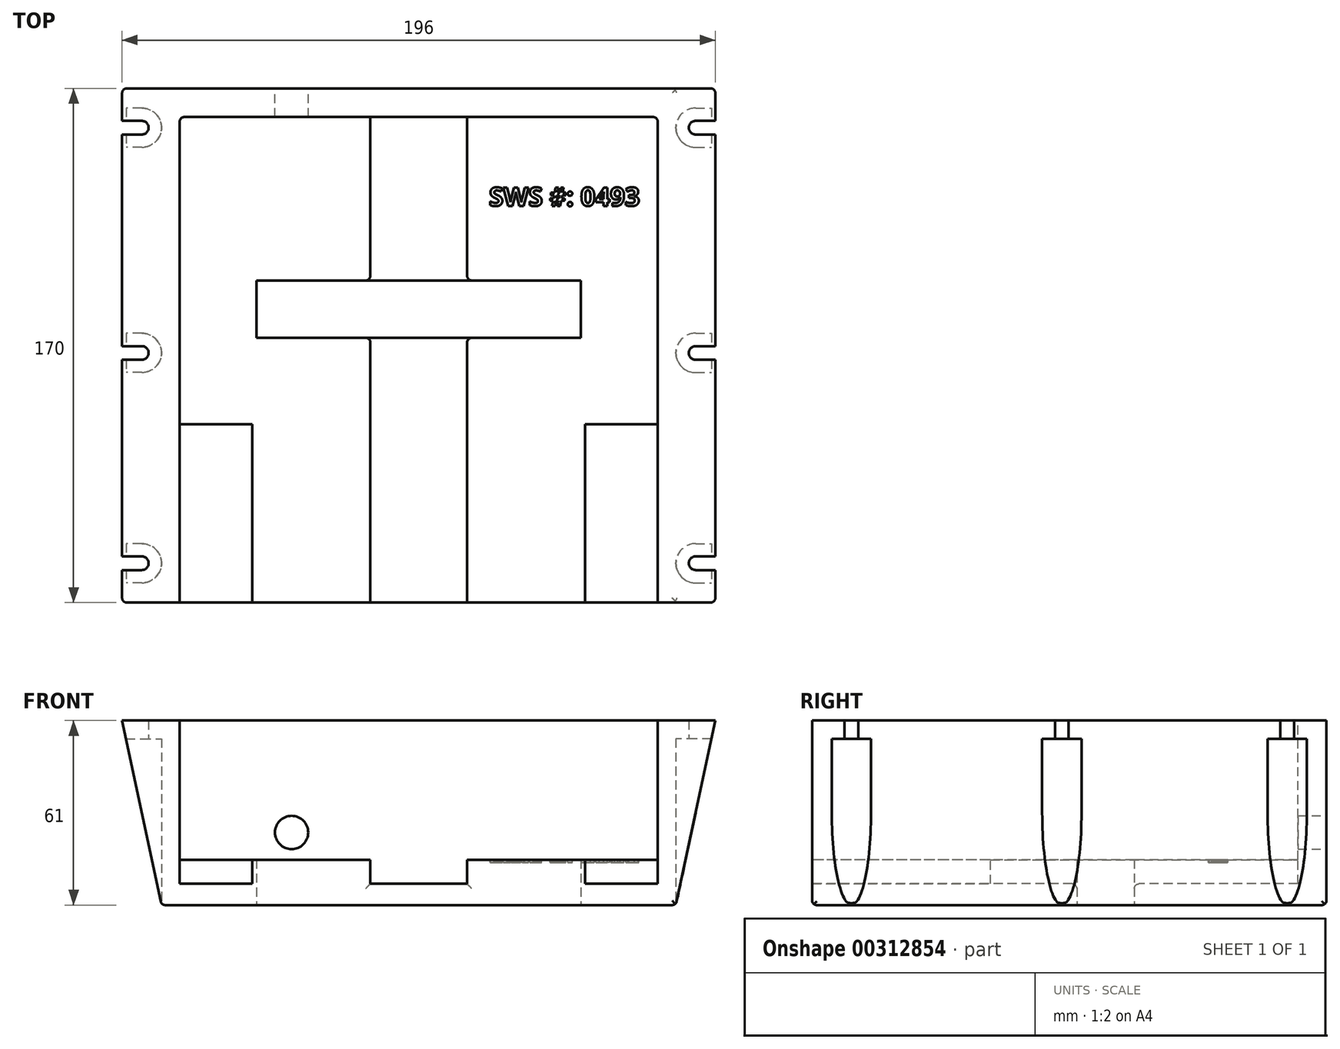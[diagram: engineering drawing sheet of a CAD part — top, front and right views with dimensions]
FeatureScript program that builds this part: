
annotation { "Feature Type Name" : "Feature", "Feature Type Description" : "" }
export const myFeature = defineFeature(function(context is Context, id is Id, definition is map)
    precondition{}
    {
        {
            var Q0;
            Q0=qCreatedBy(makeId("Top.planeOp"),FACE);
            var sketch = newSketch(context, id + "F0", { "sketchPlane" : qUnion([Q0])});
            skLineSegment(sketch, "E0.bottom", {"start": v(0, 87.46) * mm, "end": v(-85, 87.46) * mm});
            skLineSegment(sketch, "E0.top", {"start": v(0, -82.54) * mm, "end": v(-85, -82.54) * mm});
            skLineSegment(sketch, "E0.left", {"start": v(0, 87.46) * mm, "end": v(0, -82.54) * mm});
            skLineSegment(sketch, "E0.right", {"start": v(-85, 87.46) * mm, "end": v(-85, -82.54) * mm});
            skSolve(sketch);
        }
        {
            var Q0;
            Q0=makeQuery(id+"F0.imprint","IMPRINT",FACE,{"disambiguationData":[TD([[makeQuery(id+"F0.imprint","IMPRINT",EDGE,{"derivedFrom":sQuery(id+"F0.wireOp",EDGE,"E0.bottom")}),1.0]])]});
            extrude(context, id + "F1", {"entities" : qUnion([Q0]), "oppositeDirection" : true, "depth" : 61 * mm});
        }
        {
            var Q0;
            Q0=makeQuery(id+"F1.opExtrude","CAP_FACE",FACE,{"disambiguationData":[OSD([sQuery(id+"F0.wireOp",EDGE,"E0.bottom"),sQuery(id+"F0.wireOp",EDGE,"E0.top"),sQuery(id+"F0.wireOp",EDGE,"E0.left"),sQuery(id+"F0.wireOp",EDGE,"E0.right")])],"isStart":true});
            var sketch = newSketch(context, id + "F2", { "sketchPlane" : qUnion([Q0])});
            skLineSegment(sketch, "E1.bottom", {"start": v(0, -82.54) * mm, "end": v(-79, -82.54) * mm});
            skLineSegment(sketch, "E1.top", {"start": v(0, 77.96) * mm, "end": v(-79, 77.96) * mm});
            skLineSegment(sketch, "E1.left", {"start": v(0, -82.54) * mm, "end": v(0, 77.96) * mm});
            skLineSegment(sketch, "E1.right", {"start": v(-79, -82.54) * mm, "end": v(-79, 77.96) * mm});
            skSolve(sketch);
        }
        {
            var Q0;
            Q0 = qSketchRegion(id + "F2", true);
            extrude(context, id + "F3", {"entities" : qUnion([Q0]), "operationType" : NewBodyOperationType.REMOVE, "oppositeDirection" : true, "depth" : 46 * mm});
        }
        {
            var Q0;
            Q0=makeQuery(id+"F1.opExtrude","CAP_FACE",FACE,{"disambiguationData":[OSD([sQuery(id+"F0.wireOp",EDGE,"E0.bottom"),sQuery(id+"F0.wireOp",EDGE,"E0.top"),sQuery(id+"F0.wireOp",EDGE,"E0.left"),sQuery(id+"F0.wireOp",EDGE,"E0.right")])],"isStart":false});
            var sketch = newSketch(context, id + "F4", { "sketchPlane" : qUnion([Q0])});
            skLineSegment(sketch, "E2.bottom", {"start": v(0, -23.96) * mm, "end": v(-53.6, -23.96) * mm});
            skLineSegment(sketch, "E2.top", {"start": v(0, -4.96) * mm, "end": v(-53.6, -4.96) * mm});
            skLineSegment(sketch, "E2.left", {"start": v(0, -23.96) * mm, "end": v(0, -4.96) * mm});
            skLineSegment(sketch, "E2.right", {"start": v(-53.6, -23.96) * mm, "end": v(-53.6, -4.96) * mm});
            skLineSegment(sketch, "E3", {"start": v(-53.6, -23.96) * mm, "end": v(-79, -23.96) * mm, "construction": true});
            skLineSegment(sketch, "E4", {"start": v(-53.6, -4.96) * mm, "end": v(-79, -4.96) * mm, "construction": true});
            skLineSegment(sketch, "E5", {"start": v(-79, -4.96) * mm, "end": v(-79, -23.96) * mm, "construction": true});
            skSolve(sketch);
        }
        {
            var Q0;
            Q0 = qSketchRegion(id + "F4", true);
            extrude(context, id + "F5", {"entities" : qUnion([Q0]), "operationType" : NewBodyOperationType.REMOVE, "endBound" : BoundingType.UP_TO_NEXT, "oppositeDirection" : true, "depth" : 25 * mm});
        }
        {
            var Q0;
            Q0=makeQuery(id+"F3.boolean.opBoolean","COPY",FACE,{"derivedFrom":makeQuery(id+"F3.opExtrude","CAP_FACE",FACE,{"disambiguationData":[OSD([sQuery(id+"F2.wireOp",EDGE,"E1.bottom"),sQuery(id+"F2.wireOp",EDGE,"E1.top"),sQuery(id+"F2.wireOp",EDGE,"E1.left"),sQuery(id+"F2.wireOp",EDGE,"E1.right")])],"isStart":false})});
            var sketch = newSketch(context, id + "F6", { "sketchPlane" : qUnion([Q0])});
            skLineSegment(sketch, "E6.bottom", {"start": v(0, 77.96) * mm, "end": v(-16, 77.96) * mm});
            skLineSegment(sketch, "E6.top", {"start": v(0, -82.54) * mm, "end": v(-16, -82.54) * mm});
            skLineSegment(sketch, "E6.left", {"start": v(0, 77.96) * mm, "end": v(0, -82.54) * mm});
            skLineSegment(sketch, "E6.right", {"start": v(-16, 77.96) * mm, "end": v(-16, -82.54) * mm});
            skLineSegment(sketch, "E7.top", {"start": v(-79, -82.54) * mm, "end": v(-55, -82.54) * mm});
            skLineSegment(sketch, "E7.left", {"start": v(-79, -23.54) * mm, "end": v(-79, -82.54) * mm});
            skLineSegment(sketch, "E7.right", {"start": v(-55, -23.54) * mm, "end": v(-55, -82.54) * mm});
            skLineSegment(sketch, "E8", {"start": v(-55, -23.54) * mm, "end": v(-79, -23.54) * mm});
            skLineSegment(sketch, "E9", {"start": v(-55, -82.54) * mm, "end": v(-16, -82.54) * mm, "construction": true});
            skSolve(sketch);
        }
        {
            var Q0;
            Q0 = qSketchRegion(id + "F6", true);
            extrude(context, id + "F7", {"entities" : qUnion([Q0]), "operationType" : NewBodyOperationType.REMOVE, "oppositeDirection" : true, "depth" : 8 * mm});
        }
        {
            var Q0;
            Q0=makeQuery(id+"F1.opExtrude","SWEPT_FACE",FACE,{"disambiguationData":[OSD([sQuery(id+"F0.wireOp",EDGE,"E0.top")])]});
            var sketch = newSketch(context, id + "F8", { "sketchPlane" : qUnion([Q0])});
            skLineSegment(sketch, "E10", {"start": v(-85, 0) * mm, "end": v(-98, 0) * mm});
            skLineSegment(sketch, "E11", {"start": v(-98, 0) * mm, "end": v(-85, -61) * mm});
            skLineSegment(sketch, "E12", {"start": v(-85, -61) * mm, "end": v(-85, 0) * mm});
            skSolve(sketch);
        }
        {
            var Q0;
            Q0=makeQuery(id+"F8.imprint","IMPRINT",FACE,{"disambiguationData":[TD([[makeQuery(id+"F8.imprint","IMPRINT",EDGE,{"derivedFrom":sQuery(id+"F8.wireOp",EDGE,"E10")}),1.0]])]});
            var Q1;
            Q1=makeQuery(id+"F1.opExtrude","SWEPT_FACE",FACE,{"disambiguationData":[OSD([sQuery(id+"F0.wireOp",EDGE,"E0.bottom")])]});
            extrude(context, id + "F9", {"entities" : qUnion([Q0]), "operationType" : NewBodyOperationType.ADD, "endBound" : BoundingType.UP_TO_SURFACE, "oppositeDirection" : true, "endBoundEntityFace" : qUnion([Q1]), "depth" : 25 * mm});
        }
        {
            var Q0;
            Q0=makeQuery(id+"F1.opExtrude","CAP_FACE",FACE,{"disambiguationData":[OSD([sQuery(id+"F0.wireOp",EDGE,"E0.bottom"),sQuery(id+"F0.wireOp",EDGE,"E0.top"),sQuery(id+"F0.wireOp",EDGE,"E0.left"),sQuery(id+"F0.wireOp",EDGE,"E0.right")])],"isStart":false});
            var sketch = newSketch(context, id + "F10", { "sketchPlane" : qUnion([Q0])});
            skLineSegment(sketch, "E13", {"start": v(-98, -87.46) * mm, "end": v(-98, 82.54) * mm, "construction": true});
            skLineSegment(sketch, "E14", {"start": v(-85, -87.46) * mm, "end": v(-98, -87.46) * mm, "construction": true});
            skLineSegment(sketch, "E15", {"start": v(-85, 82.54) * mm, "end": v(-98, 82.54) * mm, "construction": true});
            skLineSegment(sketch, "E16", {"start": v(-91.5, -87.46) * mm, "end": v(-91.5, 82.54) * mm, "construction": true});
            skPoint(sketch, "E17", {"position": v(-91.5, 0) * mm});
            skPoint(sketch, "E18", {"position": v(-91.5, -74.46) * mm});
            skPoint(sketch, "E19", {"position": v(-91.5, 69.54) * mm});
            skArc(sketch, "E20", {"start": v(-91.5, -76.7) * mm, "mid": v(-89.25, -74.46) * mm, "end": v(-91.5, -72.2) * mm});
            skArc(sketch, "E21", {"start": v(-91.5, -2.25) * mm, "mid": v(-89.25, 0) * mm, "end": v(-91.5, 2.25) * mm});
            skArc(sketch, "E22", {"start": v(-91.5, 67.3) * mm, "mid": v(-89.25, 69.54) * mm, "end": v(-91.5, 71.8) * mm});
            skLineSegment(sketch, "E23", {"start": v(-91.5, -76.7) * mm, "end": v(-98, -76.7) * mm});
            skLineSegment(sketch, "E24", {"start": v(-91.5, -72.2) * mm, "end": v(-98, -72.2) * mm});
            skLineSegment(sketch, "E25", {"start": v(-98, -72.2) * mm, "end": v(-98, -76.7) * mm});
            skLineSegment(sketch, "E26", {"start": v(-91.5, -2.25) * mm, "end": v(-98, -2.25) * mm});
            skLineSegment(sketch, "E27", {"start": v(-91.5, 2.25) * mm, "end": v(-98, 2.25) * mm});
            skLineSegment(sketch, "E28", {"start": v(-98, 2.25) * mm, "end": v(-98, -2.25) * mm});
            skLineSegment(sketch, "E29", {"start": v(-91.5, 67.3) * mm, "end": v(-98, 67.3) * mm});
            skLineSegment(sketch, "E30", {"start": v(-91.5, 71.8) * mm, "end": v(-98, 71.8) * mm});
            skLineSegment(sketch, "E31", {"start": v(-98, 71.8) * mm, "end": v(-98, 67.3) * mm});
            skSolve(sketch);
        }
        {
            var Q0;
            Q0 = qSketchRegion(id + "F10", true);
            var Q1;
            Q1=makeQuery(id+"F9.boolean.opBoolean","MERGE",FACE,{"derivedFrom":[makeQuery(id+"F1.opExtrude","CAP_FACE",FACE,{"disambiguationData":[OSD([sQuery(id+"F0.wireOp",EDGE,"E0.bottom"),sQuery(id+"F0.wireOp",EDGE,"E0.top"),sQuery(id+"F0.wireOp",EDGE,"E0.left"),sQuery(id+"F0.wireOp",EDGE,"E0.right")])],"isStart":true}),makeQuery(id+"F9.opExtrude","SWEPT_FACE",FACE,{"disambiguationData":[OSD([sQuery(id+"F8.wireOp",EDGE,"E10")])]})]});
            extrude(context, id + "F11", {"entities" : qUnion([Q0]), "operationType" : NewBodyOperationType.REMOVE, "endBound" : BoundingType.UP_TO_SURFACE, "oppositeDirection" : true, "endBoundEntityFace" : qUnion([Q1]), "depth" : 25 * mm});
        }
        {
            var Q0;
            Q0=makeQuery(id+"F1.opExtrude","CAP_FACE",FACE,{"disambiguationData":[OSD([sQuery(id+"F0.wireOp",EDGE,"E0.bottom"),sQuery(id+"F0.wireOp",EDGE,"E0.top"),sQuery(id+"F0.wireOp",EDGE,"E0.left"),sQuery(id+"F0.wireOp",EDGE,"E0.right")])],"isStart":false});
            var sketch = newSketch(context, id + "F12", { "sketchPlane" : qUnion([Q0])});
            skLineSegment(sketch, "E32", {"start": v(-85, -87.46) * mm, "end": v(-98, -87.46) * mm, "construction": true});
            skLineSegment(sketch, "E33", {"start": v(-98, -87.46) * mm, "end": v(-98, 82.54) * mm, "construction": true});
            skLineSegment(sketch, "E34", {"start": v(-98, 82.54) * mm, "end": v(-85, 82.54) * mm, "construction": true});
            skLineSegment(sketch, "E35", {"start": v(-91.5, -87.46) * mm, "end": v(-91.5, 82.54) * mm, "construction": true});
            skArc(sketch, "E36", {"start": v(-91.5, -6.5) * mm, "mid": v(-85, 0) * mm, "end": v(-91.5, 6.5) * mm});
            skLineSegment(sketch, "E37", {"start": v(-91.5, -6.5) * mm, "end": v(-98, -6.5) * mm});
            skLineSegment(sketch, "E38", {"start": v(-91.5, 6.5) * mm, "end": v(-98, 6.5) * mm});
            skLineSegment(sketch, "E39", {"start": v(-98, 6.5) * mm, "end": v(-98, -6.5) * mm});
            skArc(sketch, "E40", {"start": v(-91.5, -80.96) * mm, "mid": v(-85, -74.46) * mm, "end": v(-91.5, -67.96) * mm});
            skLineSegment(sketch, "E41", {"start": v(-91.5, -80.96) * mm, "end": v(-98, -80.96) * mm});
            skLineSegment(sketch, "E42", {"start": v(-91.5, -67.96) * mm, "end": v(-98, -67.96) * mm});
            skLineSegment(sketch, "E43", {"start": v(-98, -67.96) * mm, "end": v(-98, -80.96) * mm});
            skArc(sketch, "E44", {"start": v(-91.5, 63.04) * mm, "mid": v(-85, 69.54) * mm, "end": v(-91.5, 76.04) * mm});
            skLineSegment(sketch, "E45", {"start": v(-91.5, 63.04) * mm, "end": v(-98, 63.04) * mm});
            skLineSegment(sketch, "E46", {"start": v(-91.5, 76.04) * mm, "end": v(-98, 76.04) * mm});
            skLineSegment(sketch, "E47", {"start": v(-98, 76.04) * mm, "end": v(-98, 63.04) * mm});
            skSolve(sketch);
        }
        {
            var Q0;
            Q0 = qSketchRegion(id + "F12", true);
            extrude(context, id + "F13", {"entities" : qUnion([Q0]), "operationType" : NewBodyOperationType.REMOVE, "oppositeDirection" : true, "depth" : 55 * mm});
        }
        {
            var Q0;
            Q0=makeQuery(id+"F1.opExtrude","SWEPT_BODY",BODY,{"disambiguationData":[OSD([sQuery(id+"F0.wireOp",EDGE,"E0.bottom"),sQuery(id+"F0.wireOp",EDGE,"E0.top"),sQuery(id+"F0.wireOp",EDGE,"E0.left"),sQuery(id+"F0.wireOp",EDGE,"E0.right")])]});
            var Q1;
            Q1=qCreatedBy(makeId("Right.planeOp"),FACE);
            mirror(context, id + "F14", {"operationType" : NewBodyOperationType.ADD, "entities" : qUnion([Q0]), "mirrorPlane" : qUnion([Q1])});
        }
        {
            var Q0;
            {var subQ0=makeQuery(id+"F1.opExtrude","CAP_EDGE",EDGE,{"disambiguationData":[OSD([sQuery(id+"F0.wireOp",EDGE,"E0.bottom")])],"isStart":false});Q0=makeQuery(id+"FNScm29ONGkGvwl_1.boolean.opBoolean","MERGE",EDGE,{"derivedFrom":[subQ0,makeQuery(id+"FNScm29ONGkGvwl_1.opPattern","COPY",EDGE,{"derivedFrom":subQ0,"instanceName":"1"})]});}
            var Q1;
            Q1=makeQuery(id+"F1.opExtrude","SWEPT_EDGE",EDGE,{"disambiguationData":[OSD([sQuery(id+"F0.wireOp",EDGE,"E0.bottom"),sQuery(id+"F0.wireOp",EDGE,"E0.right")])]});
            var Q2;
            Q2=makeQuery(id+"F1.opExtrude","CAP_EDGE",EDGE,{"disambiguationData":[OSD([sQuery(id+"F0.wireOp",EDGE,"E0.right")])],"isStart":false});
            var Q3;
            {var subQ0=makeQuery(id+"F1.opExtrude","CAP_EDGE",EDGE,{"disambiguationData":[OSD([sQuery(id+"F0.wireOp",EDGE,"E0.top")])],"isStart":false});Q3=makeQuery(id+"FNScm29ONGkGvwl_1.boolean.opBoolean","MERGE",EDGE,{"derivedFrom":[subQ0,makeQuery(id+"FNScm29ONGkGvwl_1.opPattern","COPY",EDGE,{"derivedFrom":subQ0,"instanceName":"1"})]});}
            var Q4;
            {var subQ0=makeQuery(id+"F5.boolean.opBoolean","COPY",EDGE,{"derivedFrom":makeQuery(id+"F5.opExtrude","CAP_EDGE",EDGE,{"disambiguationData":[OSD([sQuery(id+"F4.wireOp",EDGE,"E2.bottom")])],"isStart":true})});Q4=makeQuery(id+"F14.boolean.opBoolean","MERGE",EDGE,{"derivedFrom":[subQ0,makeQuery(id+"F14.opPattern","COPY",EDGE,{"derivedFrom":subQ0,"instanceName":"1"})]});}
            var Q5;
            Q5=makeQuery(id+"F5.boolean.opBoolean","COPY",EDGE,{"derivedFrom":makeQuery(id+"F5.opExtrude","CAP_EDGE",EDGE,{"disambiguationData":[OSD([sQuery(id+"F4.wireOp",EDGE,"E2.right")])],"isStart":true})});
            var Q6;
            {var subQ0=makeQuery(id+"F5.boolean.opBoolean","COPY",EDGE,{"derivedFrom":makeQuery(id+"F5.opExtrude","CAP_EDGE",EDGE,{"disambiguationData":[OSD([sQuery(id+"F4.wireOp",EDGE,"E2.top")])],"isStart":true})});Q6=makeQuery(id+"F14.boolean.opBoolean","MERGE",EDGE,{"derivedFrom":[subQ0,makeQuery(id+"F14.opPattern","COPY",EDGE,{"derivedFrom":subQ0,"instanceName":"1"})]});}
            var Q7;
            Q7=makeQuery(id+"F1.opExtrude","SWEPT_EDGE",EDGE,{"disambiguationData":[OSD([sQuery(id+"F0.wireOp",EDGE,"E0.top"),sQuery(id+"F0.wireOp",EDGE,"E0.right")])]});
            var Q8;
            {var subQ0=sQuery(id+"F2.wireOp",EDGE,"E1.top");var subQ1=sQuery(id+"F6.wireOp",EDGE,"E6.right");Q8=makeQuery(id+"F7.boolean.opBoolean","COPY",EDGE,{"disambiguationData":[TD([makeQuery(id+"F3.boolean.opBoolean","COPY",FACE,{"derivedFrom":makeQuery(id+"F3.opExtrude","SWEPT_FACE",FACE,{"disambiguationData":[OSD([subQ0])]})})])],"derivedFrom":makeQuery(id+"F7.opExtrude","CAP_EDGE",EDGE,{"disambiguationData":[OSD([subQ1])],"isStart":true})});}
            var Q9;
            {var subQ0=sQuery(id+"F6.wireOp",EDGE,"E6.right");Q9=makeQuery(id+"F7.boolean.opBoolean","COPY",EDGE,{"disambiguationData":[TD([makeQuery(id+"F1.opExtrude","SWEPT_FACE",FACE,{"disambiguationData":[OSD([sQuery(id+"F0.wireOp",EDGE,"E0.top")])]})])],"derivedFrom":makeQuery(id+"F7.opExtrude","CAP_EDGE",EDGE,{"disambiguationData":[OSD([subQ0])],"isStart":true})});}
            var Q10;
            Q10=makeQuery(id+"F7.boolean.opBoolean","COPY",EDGE,{"derivedFrom":makeQuery(id+"F7.opExtrude","CAP_EDGE",EDGE,{"disambiguationData":[OSD([sQuery(id+"F6.wireOp",EDGE,"E7.right")])],"isStart":true})});
            var Q11;
            Q11=makeQuery(id+"F3.boolean.opBoolean","COPY",EDGE,{"derivedFrom":makeQuery(id+"F3.opExtrude","CAP_EDGE",EDGE,{"disambiguationData":[OSD([sQuery(id+"F2.wireOp",EDGE,"E1.bottom")])],"isStart":false})});
            var Q12;
            {var subQ0=makeQuery(id+"F7.boolean.opBoolean","COPY",EDGE,{"derivedFrom":makeQuery(id+"F7.opExtrude","CAP_EDGE",EDGE,{"disambiguationData":[OSD([sQuery(id+"F6.wireOp",EDGE,"E6.top")])],"isStart":false})});Q12=makeQuery(id+"FNScm29ONGkGvwl_1.boolean.opBoolean","MERGE",EDGE,{"derivedFrom":[subQ0,makeQuery(id+"FNScm29ONGkGvwl_1.opPattern","COPY",EDGE,{"derivedFrom":subQ0,"instanceName":"1"})]});}
            var Q13;
            Q13=makeQuery(id+"F7.boolean.opBoolean","COPY",EDGE,{"derivedFrom":makeQuery(id+"F7.opExtrude","SWEPT_EDGE",EDGE,{"disambiguationData":[OSD([sQuery(id+"F2.wireOp",EDGE,"E1.bottom"),sQuery(id+"F6.wireOp",EDGE,"E6.top"),sQuery(id+"F6.wireOp",EDGE,"E6.right")])]})});
            var Q14;
            Q14=makeQuery(id+"F7.boolean.opBoolean","COPY",EDGE,{"derivedFrom":makeQuery(id+"F7.opExtrude","SWEPT_EDGE",EDGE,{"disambiguationData":[OSD([sQuery(id+"F2.wireOp",EDGE,"E1.bottom"),sQuery(id+"F6.wireOp",EDGE,"E7.top"),sQuery(id+"F6.wireOp",EDGE,"E7.right")])]})});
            var Q15;
            Q15=makeQuery(id+"F7.boolean.opBoolean","COPY",EDGE,{"derivedFrom":makeQuery(id+"F7.opExtrude","CAP_EDGE",EDGE,{"disambiguationData":[OSD([sQuery(id+"F6.wireOp",EDGE,"E7.top")])],"isStart":false})});
            var Q16;
            Q16=makeQuery(id+"F7.boolean.opBoolean","MERGE",EDGE,{"derivedFrom":[makeQuery(id+"F3.boolean.opBoolean","COPY",EDGE,{"derivedFrom":makeQuery(id+"F3.opExtrude","SWEPT_EDGE",EDGE,{"disambiguationData":[OSD([sQuery(id+"F0.wireOp",EDGE,"E0.top"),sQuery(id+"F2.wireOp",EDGE,"E1.bottom"),sQuery(id+"F2.wireOp",EDGE,"E1.right")])]})}),makeQuery(id+"F7.opExtrude","SWEPT_EDGE",EDGE,{"disambiguationData":[OSD([sQuery(id+"F6.wireOp",EDGE,"E7.top"),sQuery(id+"F6.wireOp",EDGE,"E7.left")])]})]});
            var Q17;
            Q17=makeQuery(id+"F14.opPattern","COPY",EDGE,{"derivedFrom":makeQuery(id+"F9.opExtrude","CAP_EDGE",EDGE,{"disambiguationData":[OSD([sQuery(id+"F8.wireOp",EDGE,"E11")])],"isStart":false}),"instanceName":"1"});
            var Q18;
            Q18=makeQuery(id+"F9.opExtrude","CAP_EDGE",EDGE,{"disambiguationData":[OSD([sQuery(id+"F8.wireOp",EDGE,"E11")])],"isStart":false});
            var Q19;
            Q19=makeQuery(id+"F9.opExtrude","CAP_EDGE",EDGE,{"disambiguationData":[OSD([sQuery(id+"F8.wireOp",EDGE,"E11")])],"isStart":true});
            var Q20;
            Q20=makeQuery(id+"F14.opPattern","COPY",EDGE,{"derivedFrom":makeQuery(id+"F9.opExtrude","CAP_EDGE",EDGE,{"disambiguationData":[OSD([sQuery(id+"F8.wireOp",EDGE,"E11")])],"isStart":true}),"instanceName":"1"});
            var Q21;
            {var subQ0=sQuery(id+"F0.wireOp",EDGE,"E0.right");var subQ1=sQuery(id+"F0.wireOp",EDGE,"E0.top");var subQ2=sQuery(id+"F8.wireOp",EDGE,"E11");Q21=makeQuery(id+"F14.opPattern","COPY",EDGE,{"derivedFrom":makeQuery(id+"F13.boolean.opBoolean","SPLIT",EDGE,{"disambiguationData":[TD([makeQuery(id+"F1.opExtrude","CAP_FACE",FACE,{"disambiguationData":[OSD([sQuery(id+"F0.wireOp",EDGE,"E0.bottom"),subQ1,sQuery(id+"F0.wireOp",EDGE,"E0.left"),subQ0])],"isStart":false}),makeQuery(id+"F9.opExtrude","SWEPT_FACE",FACE,{"disambiguationData":[OSD([subQ2])]}),makeQuery(id+"F13.opExtrude","SWEPT_FACE",FACE,{"disambiguationData":[OSD([sQuery(id+"F12.wireOp",EDGE,"E36")])]}),makeQuery(id+"F13.opExtrude","SWEPT_FACE",FACE,{"disambiguationData":[OSD([sQuery(id+"F12.wireOp",EDGE,"E40")])]})])],"derivedFrom":makeQuery(id+"F9.boolean.opBoolean","MERGE",EDGE,{"derivedFrom":[makeQuery(id+"F1.opExtrude","CAP_EDGE",EDGE,{"disambiguationData":[OSD([subQ0])],"isStart":false}),makeQuery(id+"F9.opExtrude","SWEPT_EDGE",EDGE,{"disambiguationData":[OSD([subQ1,subQ2,sQuery(id+"F8.wireOp",EDGE,"E12")])]})]})}),"instanceName":"1"});}
            var Q22;
            Q22=makeQuery(id+"F14.opPattern","COPY",EDGE,{"derivedFrom":makeQuery(id+"F3.boolean.opBoolean","COPY",EDGE,{"derivedFrom":makeQuery(id+"F3.opExtrude","CAP_EDGE",EDGE,{"disambiguationData":[OSD([sQuery(id+"F2.wireOp",EDGE,"E1.bottom")])],"isStart":false})}),"instanceName":"1"});
            var Q23;
            Q23=makeQuery(id+"F14.opPattern","COPY",EDGE,{"derivedFrom":makeQuery(id+"F7.boolean.opBoolean","COPY",EDGE,{"derivedFrom":makeQuery(id+"F7.opExtrude","SWEPT_EDGE",EDGE,{"disambiguationData":[OSD([sQuery(id+"F2.wireOp",EDGE,"E1.bottom"),sQuery(id+"F6.wireOp",EDGE,"E6.top"),sQuery(id+"F6.wireOp",EDGE,"E6.right")])]})}),"instanceName":"1"});
            var Q24;
            Q24=makeQuery(id+"F14.opPattern","COPY",EDGE,{"derivedFrom":makeQuery(id+"F7.boolean.opBoolean","COPY",EDGE,{"derivedFrom":makeQuery(id+"F7.opExtrude","SWEPT_EDGE",EDGE,{"disambiguationData":[OSD([sQuery(id+"F2.wireOp",EDGE,"E1.bottom"),sQuery(id+"F6.wireOp",EDGE,"E7.top"),sQuery(id+"F6.wireOp",EDGE,"E7.right")])]})}),"instanceName":"1"});
            var Q25;
            Q25=makeQuery(id+"F14.opPattern","COPY",EDGE,{"derivedFrom":makeQuery(id+"F7.boolean.opBoolean","COPY",EDGE,{"derivedFrom":makeQuery(id+"F7.opExtrude","CAP_EDGE",EDGE,{"disambiguationData":[OSD([sQuery(id+"F6.wireOp",EDGE,"E7.top")])],"isStart":false})}),"instanceName":"1"});
            var Q26;
            Q26=makeQuery(id+"F14.opPattern","COPY",EDGE,{"derivedFrom":makeQuery(id+"F7.boolean.opBoolean","MERGE",EDGE,{"derivedFrom":[makeQuery(id+"F3.boolean.opBoolean","COPY",EDGE,{"derivedFrom":makeQuery(id+"F3.opExtrude","SWEPT_EDGE",EDGE,{"disambiguationData":[OSD([sQuery(id+"F0.wireOp",EDGE,"E0.top"),sQuery(id+"F2.wireOp",EDGE,"E1.bottom"),sQuery(id+"F2.wireOp",EDGE,"E1.right")])]})}),makeQuery(id+"F7.opExtrude","SWEPT_EDGE",EDGE,{"disambiguationData":[OSD([sQuery(id+"F6.wireOp",EDGE,"E7.top"),sQuery(id+"F6.wireOp",EDGE,"E7.left")])]})]}),"instanceName":"1"});
            var Q27;
            Q27=makeQuery(id+"F14.opPattern","COPY",EDGE,{"derivedFrom":makeQuery(id+"F5.boolean.opBoolean","COPY",EDGE,{"derivedFrom":makeQuery(id+"F5.opExtrude","CAP_EDGE",EDGE,{"disambiguationData":[OSD([sQuery(id+"F4.wireOp",EDGE,"E2.right")])],"isStart":true})}),"instanceName":"1"});
            var Q28;
            Q28=makeQuery(id+"F14.opPattern","COPY",EDGE,{"derivedFrom":makeQuery(id+"F7.boolean.opBoolean","COPY",EDGE,{"derivedFrom":makeQuery(id+"F7.opExtrude","CAP_EDGE",EDGE,{"disambiguationData":[OSD([sQuery(id+"F6.wireOp",EDGE,"E7.right")])],"isStart":true})}),"instanceName":"1"});
            var Q29;
            {var subQ0=sQuery(id+"F6.wireOp",EDGE,"E6.right");Q29=makeQuery(id+"F14.opPattern","COPY",EDGE,{"derivedFrom":makeQuery(id+"F7.boolean.opBoolean","COPY",EDGE,{"disambiguationData":[TD([makeQuery(id+"F1.opExtrude","SWEPT_FACE",FACE,{"disambiguationData":[OSD([sQuery(id+"F0.wireOp",EDGE,"E0.top")])]})])],"derivedFrom":makeQuery(id+"F7.opExtrude","CAP_EDGE",EDGE,{"disambiguationData":[OSD([subQ0])],"isStart":true})}),"instanceName":"1"});}
            var Q30;
            {var subQ0=sQuery(id+"F2.wireOp",EDGE,"E1.top");var subQ1=sQuery(id+"F6.wireOp",EDGE,"E6.right");Q30=makeQuery(id+"F14.opPattern","COPY",EDGE,{"derivedFrom":makeQuery(id+"F7.boolean.opBoolean","COPY",EDGE,{"disambiguationData":[TD([makeQuery(id+"F3.boolean.opBoolean","COPY",FACE,{"derivedFrom":makeQuery(id+"F3.opExtrude","SWEPT_FACE",FACE,{"disambiguationData":[OSD([subQ0])]})})])],"derivedFrom":makeQuery(id+"F7.opExtrude","CAP_EDGE",EDGE,{"disambiguationData":[OSD([subQ1])],"isStart":true})}),"instanceName":"1"});}
            var Q31;
            Q31=makeQuery(id+"F14.opPattern","COPY",EDGE,{"derivedFrom":makeQuery(id+"F5.boolean.opBoolean","COPY",EDGE,{"derivedFrom":makeQuery(id+"F5.opExtrude","CAP_EDGE",EDGE,{"disambiguationData":[OSD([sQuery(id+"F4.wireOp",EDGE,"E2.bottom")])],"isStart":false})}),"instanceName":"1"});
            var Q32;
            Q32=makeQuery(id+"F5.boolean.opBoolean","COPY",EDGE,{"derivedFrom":makeQuery(id+"F5.opExtrude","CAP_EDGE",EDGE,{"disambiguationData":[OSD([sQuery(id+"F4.wireOp",EDGE,"E2.bottom")])],"isStart":false})});
            var Q33;
            Q33=makeQuery(id+"F5.boolean.opBoolean","COPY",EDGE,{"derivedFrom":makeQuery(id+"F5.opExtrude","CAP_EDGE",EDGE,{"disambiguationData":[OSD([sQuery(id+"F4.wireOp",EDGE,"E2.right")])],"isStart":false})});
            var Q34;
            Q34=makeQuery(id+"F5.boolean.opBoolean","COPY",EDGE,{"derivedFrom":makeQuery(id+"F5.opExtrude","CAP_EDGE",EDGE,{"disambiguationData":[OSD([sQuery(id+"F4.wireOp",EDGE,"E2.top")])],"isStart":false})});
            var Q35;
            Q35=makeQuery(id+"F14.opPattern","COPY",EDGE,{"derivedFrom":makeQuery(id+"F5.boolean.opBoolean","COPY",EDGE,{"derivedFrom":makeQuery(id+"F5.opExtrude","CAP_EDGE",EDGE,{"disambiguationData":[OSD([sQuery(id+"F4.wireOp",EDGE,"E2.top")])],"isStart":false})}),"instanceName":"1"});
            var Q36;
            Q36=makeQuery(id+"F14.opPattern","COPY",EDGE,{"derivedFrom":makeQuery(id+"F5.boolean.opBoolean","COPY",EDGE,{"derivedFrom":makeQuery(id+"F5.opExtrude","CAP_EDGE",EDGE,{"disambiguationData":[OSD([sQuery(id+"F4.wireOp",EDGE,"E2.right")])],"isStart":false})}),"instanceName":"1"});
            var Q37;
            Q37=makeQuery(id+"F14.opPattern","COPY",EDGE,{"derivedFrom":makeQuery(id+"F7.boolean.opBoolean","INTERSECT",EDGE,{"derivedFrom":[makeQuery(id+"F5.boolean.opBoolean","COPY",FACE,{"derivedFrom":makeQuery(id+"F5.opExtrude","SWEPT_FACE",FACE,{"disambiguationData":[OSD([sQuery(id+"F4.wireOp",EDGE,"E2.top")])]})}),makeQuery(id+"F7.opExtrude","SWEPT_FACE",FACE,{"disambiguationData":[OSD([sQuery(id+"F6.wireOp",EDGE,"E6.right")])]})]}),"instanceName":"1"});
            var Q38;
            Q38=makeQuery(id+"F7.boolean.opBoolean","INTERSECT",EDGE,{"derivedFrom":[makeQuery(id+"F5.boolean.opBoolean","COPY",FACE,{"derivedFrom":makeQuery(id+"F5.opExtrude","SWEPT_FACE",FACE,{"disambiguationData":[OSD([sQuery(id+"F4.wireOp",EDGE,"E2.top")])]})}),makeQuery(id+"F7.opExtrude","SWEPT_FACE",FACE,{"disambiguationData":[OSD([sQuery(id+"F6.wireOp",EDGE,"E6.right")])]})]});
            var Q39;
            Q39=makeQuery(id+"F7.boolean.opBoolean","INTERSECT",EDGE,{"derivedFrom":[makeQuery(id+"F5.boolean.opBoolean","COPY",FACE,{"derivedFrom":makeQuery(id+"F5.opExtrude","SWEPT_FACE",FACE,{"disambiguationData":[OSD([sQuery(id+"F4.wireOp",EDGE,"E2.bottom")])]})}),makeQuery(id+"F7.opExtrude","SWEPT_FACE",FACE,{"disambiguationData":[OSD([sQuery(id+"F6.wireOp",EDGE,"E6.right")])]})]});
            var Q40;
            Q40=makeQuery(id+"F14.opPattern","COPY",EDGE,{"derivedFrom":makeQuery(id+"F7.boolean.opBoolean","INTERSECT",EDGE,{"derivedFrom":[makeQuery(id+"F5.boolean.opBoolean","COPY",FACE,{"derivedFrom":makeQuery(id+"F5.opExtrude","SWEPT_FACE",FACE,{"disambiguationData":[OSD([sQuery(id+"F4.wireOp",EDGE,"E2.bottom")])]})}),makeQuery(id+"F7.opExtrude","SWEPT_FACE",FACE,{"disambiguationData":[OSD([sQuery(id+"F6.wireOp",EDGE,"E6.right")])]})]}),"instanceName":"1"});
            var Q41;
            {var subQ0=makeQuery(id+"F7.boolean.opBoolean","INTERSECT",EDGE,{"derivedFrom":[makeQuery(id+"F5.boolean.opBoolean","COPY",FACE,{"derivedFrom":makeQuery(id+"F5.opExtrude","SWEPT_FACE",FACE,{"disambiguationData":[OSD([sQuery(id+"F4.wireOp",EDGE,"E2.top")])]})}),makeQuery(id+"F7.opExtrude","CAP_FACE",FACE,{"disambiguationData":[OSD([sQuery(id+"F6.wireOp",EDGE,"E6.bottom"),sQuery(id+"F6.wireOp",EDGE,"E6.top"),sQuery(id+"F6.wireOp",EDGE,"E6.left"),sQuery(id+"F6.wireOp",EDGE,"E6.right")])],"isStart":false})]});Q41=makeQuery(id+"F14.boolean.opBoolean","MERGE",EDGE,{"derivedFrom":[subQ0,makeQuery(id+"F14.opPattern","COPY",EDGE,{"derivedFrom":subQ0,"instanceName":"1"})]});}
            var Q42;
            {var subQ0=makeQuery(id+"F7.boolean.opBoolean","INTERSECT",EDGE,{"derivedFrom":[makeQuery(id+"F5.boolean.opBoolean","COPY",FACE,{"derivedFrom":makeQuery(id+"F5.opExtrude","SWEPT_FACE",FACE,{"disambiguationData":[OSD([sQuery(id+"F4.wireOp",EDGE,"E2.bottom")])]})}),makeQuery(id+"F7.opExtrude","CAP_FACE",FACE,{"disambiguationData":[OSD([sQuery(id+"F6.wireOp",EDGE,"E6.bottom"),sQuery(id+"F6.wireOp",EDGE,"E6.top"),sQuery(id+"F6.wireOp",EDGE,"E6.left"),sQuery(id+"F6.wireOp",EDGE,"E6.right")])],"isStart":false})]});Q42=makeQuery(id+"F14.boolean.opBoolean","MERGE",EDGE,{"derivedFrom":[subQ0,makeQuery(id+"F14.opPattern","COPY",EDGE,{"derivedFrom":subQ0,"instanceName":"1"})]});}
            var Q43;
            Q43=makeQuery(id+"F7.boolean.opBoolean","MERGE",EDGE,{"derivedFrom":[makeQuery(id+"F3.boolean.opBoolean","COPY",EDGE,{"derivedFrom":makeQuery(id+"F3.opExtrude","SWEPT_EDGE",EDGE,{"disambiguationData":[OSD([sQuery(id+"F2.wireOp",EDGE,"E1.top"),sQuery(id+"F2.wireOp",EDGE,"E1.right")])]})}),makeQuery(id+"F7.opExtrude","SWEPT_EDGE",EDGE,{"disambiguationData":[OSD([sQuery(id+"F6.wireOp",EDGE,"E7.bottom"),sQuery(id+"F6.wireOp",EDGE,"E7.left")])]})]});
            var Q44;
            Q44=makeQuery(id+"F14.opPattern","COPY",EDGE,{"derivedFrom":makeQuery(id+"F7.boolean.opBoolean","MERGE",EDGE,{"derivedFrom":[makeQuery(id+"F3.boolean.opBoolean","COPY",EDGE,{"derivedFrom":makeQuery(id+"F3.opExtrude","SWEPT_EDGE",EDGE,{"disambiguationData":[OSD([sQuery(id+"F2.wireOp",EDGE,"E1.top"),sQuery(id+"F2.wireOp",EDGE,"E1.right")])]})}),makeQuery(id+"F7.opExtrude","SWEPT_EDGE",EDGE,{"disambiguationData":[OSD([sQuery(id+"F6.wireOp",EDGE,"E7.bottom"),sQuery(id+"F6.wireOp",EDGE,"E7.left")])]})]}),"instanceName":"1"});
            fillet(context, id + "F15", {"entities" : qUnion([Q0, Q1, Q2, Q3, Q4, Q5, Q6, Q7, Q8, Q9, Q10, Q11, Q12, Q13, Q14, Q15, Q16, Q17, Q18, Q19, Q20, Q21, Q22, Q23, Q24, Q25, Q26, Q27, Q28, Q29, Q30, Q31, Q32, Q33, Q34, Q35, Q36, Q37, Q38, Q39, Q40, Q41, Q42, Q43, Q44]), "radius" : 1.5 * mm, "tangentPropagation" : true, "allowEdgeOverflow" : false});
        }
        {
            var Q0;
            {var subQ0=makeQuery(id+"F9.boolean.opBoolean","MERGE",FACE,{"derivedFrom":[makeQuery(id+"F1.opExtrude","SWEPT_FACE",FACE,{"disambiguationData":[OSD([sQuery(id+"F0.wireOp",EDGE,"E0.bottom")])]}),makeQuery(id+"F9.opExtrude","CAP_FACE",FACE,{"disambiguationData":[OSD([sQuery(id+"F8.wireOp",EDGE,"E10"),sQuery(id+"F8.wireOp",EDGE,"E11"),sQuery(id+"F8.wireOp",EDGE,"E12")])],"isStart":false})]});Q0=makeQuery(id+"F14.boolean.opBoolean","MERGE",FACE,{"derivedFrom":[subQ0,makeQuery(id+"F14.opPattern","COPY",FACE,{"derivedFrom":subQ0,"instanceName":"1"})]});}
            var sketch = newSketch(context, id + "F16", { "sketchPlane" : qUnion([Q0])});
            skPoint(sketch, "E48", {"position": v(25, -23) * mm});
            skPoint(sketch, "E49", {"position": v(42, -37) * mm});
            skSolve(sketch);
        }
        {
            var Q0;
            Q0=sQuery(id+"F16.wireOp",VERTEX,"E49");
            var Q1;
            Q1=makeQuery(id+"F1.opExtrude","SWEPT_BODY",BODY,{"disambiguationData":[OSD([sQuery(id+"F0.wireOp",EDGE,"E0.bottom"),sQuery(id+"F0.wireOp",EDGE,"E0.top"),sQuery(id+"F0.wireOp",EDGE,"E0.left"),sQuery(id+"F0.wireOp",EDGE,"E0.right")])]});
            hole(context, id + "F17", {"style" : HoleStyle.SIMPLE, "endStyle" : HoleEndStyle.THROUGH, "holeDiameter" : 11 * mm, "isTappedThrough" : true, "tappedDepth" : 12 * mm, "tapClearance" : 3, "startFromSketch" : true, "locations" : qUnion([Q0]), "scope" : qUnion([Q1])});
        }
        {
            var Q0;
            Q0=makeQuery(id+"F14.opPattern","COPY",FACE,{"derivedFrom":makeQuery(id+"F3.boolean.opBoolean","COPY",FACE,{"derivedFrom":makeQuery(id+"F3.opExtrude","CAP_FACE",FACE,{"disambiguationData":[OSD([sQuery(id+"F2.wireOp",EDGE,"E1.bottom"),sQuery(id+"F2.wireOp",EDGE,"E1.top"),sQuery(id+"F2.wireOp",EDGE,"E1.left"),sQuery(id+"F2.wireOp",EDGE,"E1.right")])],"isStart":false})}),"instanceName":"1"});
            var sketch = newSketch(context, id + "F18", { "sketchPlane" : qUnion([Q0])});
            skText(sketch, "E50", { "text": "SWS #: 0493", "fontName": "OpenSans-Bold.ttf"});
            skLineSegment(sketch, "E51", {"start": v(48.25, 77.96) * mm, "end": v(48.25, 25.46) * mm, "construction": true});
            const initialGuessF18  = {"E50": [0.02325, 0.04858, 1, 0, 0.00618]};
            skSetInitialGuess(sketch, initialGuessF18);
            skSolve(sketch);
        }
        {
            var Q0;
            Q0 = qSketchRegion(id + "F18", true);
            extrude(context, id + "F19", {"entities" : qUnion([Q0]), "operationType" : NewBodyOperationType.REMOVE, "oppositeDirection" : true, "depth" : 1 * mm});
        }
    });
